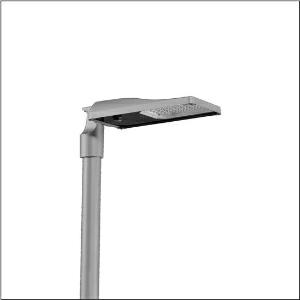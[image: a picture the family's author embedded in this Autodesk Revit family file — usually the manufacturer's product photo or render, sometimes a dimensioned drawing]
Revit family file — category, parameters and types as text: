
# Revit family: streetlight_sl_31_mini___st1_0a_5xh6d31r08ja_5198
name_source: partatom
category: Lighting Fixtures
units: mm (PartAtom-declared; Revit-internal decimal feet)

## family parameters
Cut with Voids When Loaded = No
Host = Face
Light Source = No
Part Type = Normal
Room Calculation Point = No
Round Connector Dimension = Use Diameter
Shared = No

## types (1)
- --- (1 x LED, 12270 lm, 82.5 W, 3000K)
    Apparent Load = 83 VA
    CIE Flux Codes = 40 73 97 100 100
    Color Rendering = 70
    Color Temperature = 3000K
    Default Elevation = 1800 mm
    Description = Streetlight SL 31 mini, mast luminaire, primary light control with lens, of PMMA, primary optical cover: cover, of toughened safety glass, transparent, light distribution: ST1.0a, light emission: direct distribution, primary light characteristic: asymmetric, installation type: post-top, side-entry, LED, High Power LED, rated luminous flux: 12.270lm, luminous efficacy: 149lm/W, light colour: 730, colour temperature: 3000K, control: presetting dimming logarithmic, flexible luminous flux parameterisation, time-dependent luminous flux control, constant luminous flux control, power reduction, intelligent temperature release in ECG and LED module, overheat protection, with cable H07RN-F 2x 1.5mm², mains connection: 220..240V, AC, 50/60Hz, connection cable pre-assembled, cable length: 10,5m, start of lifetime: 83W, end of service life: 90W, reduction: 37W, luminaire housing, of diecast aluminium, powder-coated, Siteco® metallic grey (DB 702S), corrosivity category C5 high according to DIN EN ISO 12944, sealing non-destructively replaceable, multi-level sealing system, mast flange (76/60mm) included as standard, inclination: -15°..+20° (post-top) | -20°..+20° (side-entry), adjustable in 5° steps, no sealing on luminaire upper side, Smart Interface below, protection rating (complete): IP66, insulation class (complete): insulation class II (safety insulation), certification: CE, ENEC, ENEC+, VDE, UKCA, ZD4i, impact resistance: IK09, permissible operating ambient temperature for outdoor applications: -40..+50°C, standard-compliant lighting for roads and squares, packaging unit: 1 piece

Light Distribution: ST1.0a
    Height = 76 mm
    Lamp = 1 x LED
    Lamp Light Flux = 12270 lm
    Lamp Power = 82.5 W
    Lamp count = 1
    Length = 547 mm
    Luminous efficacy = 149 lm/W
    Manufacturer = Siteco
    ModVariant = No
    Model = 5XH6D31R08JA
    Number of Poles = 1
    OnlyDefault = Yes
    Power Factor = 1
    Product Name = Streetlight SL 31 mini | ST1.0a
    Product group = mast luminaire | pylon top
    ProductGroupID = 6100
    Protection Class = Protection class II
    Protection Degree = IP 66
    RLX_Detail_Level = 1
    RLX_Emergency_Light_Flux = 0 lm
    RLX_Emergency_Type = 0
    RLX_Emergency_Type_DB = No
    RlxData = <blob elided: 40137 chars, md5=c25bf517>
    Socket = socket
    Standby Power = 0 W
    System Light Flux = 12270 lm
    System Power = 83 W
    Type Comments = factory setting: luminous flux: 100 % | dim-lin: 254 | 870 mA
    Type Image = l_1300328.jpg
    URL = http://relux.com
    VarID = @adj_007975
    Voltage = 0 V
    Weight = 0.00 kg
    Width = 265 mm

## geometry (parser evidence)
native form markers: Blend x4, Sweep x9
no freeform markers — native parametric forms only
